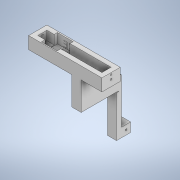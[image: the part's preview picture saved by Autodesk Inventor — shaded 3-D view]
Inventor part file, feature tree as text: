
AUTODESK INVENTOR PART (.ipt)
format: ipt  version: 2020 (Build 240168000, 168)  size: 455,168 bytes
history: native  units: in
note: dims shown in document units (in); Inventor stores cm internally (conversion verified against a paired STEP export)
features: sketch x15, extrude x14, fillet x1, emboss x1
ambient origin geometry x8: Origin, YZ Plane, XZ Plane, XY Plane, X Axis, Y Axis, Z Axis, Center Point
bodies: Solid1 (feature_tree)
feature tree (31):
  extrude  "Extrusion1"  Depth=1.5in
  extrude  "Extrusion2"  Depth=0.375in
  extrude  "Extrusion3"  Depth=0.375in
  extrude  "Extrusion4"  Depth=0.75in TaperAngle=0.0deg
  extrude  "Extrusion5"  Depth=7.5625in TaperAngle=0.0deg
  extrude  "Extrusion6"  Depth=0.141in
  extrude  "Extrusion7"  Depth=0.77in
  extrude  "Extrusion8"  Depth=0.141in
  fillet  "Fillet1"  Radius=0.141in
  extrude  "Extrusion9"  Depth=0.25in
  extrude  "Extrusion10"  Depth=1.8in TaperAngle=0.0deg
  extrude  "Extrusion13"  Depth=0.0625in
  extrude  "Extrusion14"  Depth=0.5in TaperAngle=0.0deg
  extrude  "Extrusion15"  Depth=0.75in
  extrude  "Extrusion16"  Depth=0.75in TaperAngle=0.0deg
  emboss  "Emboss1"
  sketch  "Sketch1"  dims[d0=6.0in d1=1.5in]
  sketch  "Sketch3"  dims[d2=1.0in d3=0.0in d4=0.375in]
  sketch  "Sketch4"  dims[d5=0.375in d6=0.375in]
  sketch  "Sketch5"  dims[d7=0.375in d8=0.75in d9=0.0in]
  sketch  "Sketch6"  dims[d13=7.5625in d14=0.0in d20=7.5625in d21=0.0in]
  sketch  "Sketch7"  dims[d22=0.8in d23=0.0in d24=0.141in]
  sketch  "Sketch8"  dims[d25=0.141in d31=0.77in]
  sketch  "Sketch9"  dims[d32=0.141in d33=0.141in d34=0.141in]
  sketch  "Sketch10"  dims[d35=0.141in d36=0.25in]
  sketch  "Sketch11"  dims[d37=2.3in d38=0.0in d39=1.8in d40=0.0in]
  sketch  "Sketch14"  dims[d41=3.0in d42=0.0in d43=0.0625in]
  sketch  "Sketch15"  dims[d44=0.25in d45=0.0in d46=0.5in d47=0.0in]
  sketch  "Sketch16"  dims[d55=0.446in d56=0.0in d57=0.75in]
  sketch  "Sketch17"  dims[d58=0.75in d59=0.75in d60=0.0in]
  sketch  "Sketch18"  dims[d61=0.141in d62=1.5625in d63=0.0in d64=0.156in d65=0.0in d66=0.1in d67=0.0in]
